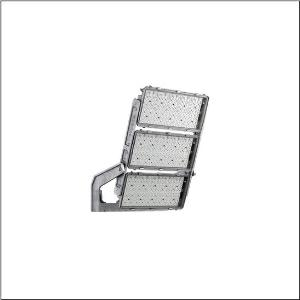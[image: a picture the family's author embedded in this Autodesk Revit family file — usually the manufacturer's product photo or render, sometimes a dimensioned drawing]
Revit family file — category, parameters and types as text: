
# Revit family: floodlight_fl_11_maxi_pro_remote___pl64blc_5xa779428w01aa_23f9
name_source: partatom
category: Lighting Fixtures
units: mm (PartAtom-declared; Revit-internal decimal feet)

## family parameters
Cut with Voids When Loaded = No
Host = Face
Light Source = No
Part Type = Normal
Room Calculation Point = No
Round Connector Dimension = Use Diameter
Shared = No

## types (1)
- --- (1 x LED, 127830 lm, 1516.9 W, 5700K)
    Apparent Load = 1517 VA
    CIE Flux Codes = 28 83 99 100 100
    Color Rendering = 80
    Color Temperature = 5700K
    Default Elevation = 1800 mm
    Description = Floodlight FL 11  maxi  pro Remote floodlight; light control with lens of PMMA; cover panel of toughened safety glass, transparent; light distribution: PL64BLC, asymmetric direct distribution, LEDcolour temperature: 5700K, rated luminous flux: 127.830lm, colour rendering: CRI > 80, light colour: 857; luminous efficacy: 84lm/W; brightness control: DALI 2 (1 DALI address); with terminal, 8-pole, max. 2.5mm², mains connection: 220..240V/380..400V AC, 50/60Hz, surge voltage resistance: line to ground: 10kV, dimming range 10..100%, dustproof LED module, LED unit replaceable without ESD environment, no afterglow with DALI off / DMX off command, ECG replaceable separately; 1517W floodlight with 3x LED unit of diecast aluminium, coated grey; length: 1.003mm / width: 651mm / height: 338mm; mounting bracket, of diecast aluminium, uncoated, natural, equipment: Power, protection rating (complete): IP66; insulation class (complete): insulation class I (protective earthing); certification: CE, ENEC, VDE; ball protection: ball impact resistant, impact resistance: IK07; only for outdoor installations, rated ambient temperature 10°C, permissible operating ambient temperature: -40..+30°C, permissible storage temperature: -40..+85°C; packaging unit: 1 piece

Light Distribution: PL64BLC
    Height = 320 mm
    Lamp = 1 x LED
    Lamp Light Flux = 127830 lm
    Lamp Power = 1516.9 W
    Lamp count = 1
    Length = 1002 mm
    Luminous efficacy = 84 lm/W
    Manufacturer = Siteco
    ModVariant = No
    Model = 5XA779428W01AA
    Mounting Place = Ceiling
    Mounting Type = Surface mounted
    Number of Poles = 1
    OnlyDefault = Yes
    Power Factor = 1
    Product Name = Floodlight FL 11 maxi pro Remote | PL64BLC
    Product group = floodlight | ceiling mounted
    ProductGroupID = 303
    Protection Class = Protection class I
    Protection Degree = IP 66
    RLX_Detail_Level = 1
    RLX_Emergency_Light_Flux = 0 lm
    RLX_Emergency_Type = 0
    RLX_Emergency_Type_DB = No
    RlxData = <blob elided: 52109 chars, md5=0c94131f>
    Socket = socket
    Standby Power = 0 W
    System Light Flux = 127830 lm
    System Power = 1517 W
    Type Comments = factory setting: luminous flux: 100 % | dim-lin: 254 | 1070 mA
    Type Image = l_1006784.jpg
    URL = http://relux.com
    VarID = @adj_032457
    Voltage = 0 V
    Weight = 0.00 kg
    Width = 655 mm

## geometry (parser evidence)
native form markers: Blend x4, Sweep x13
no freeform markers — native parametric forms only
